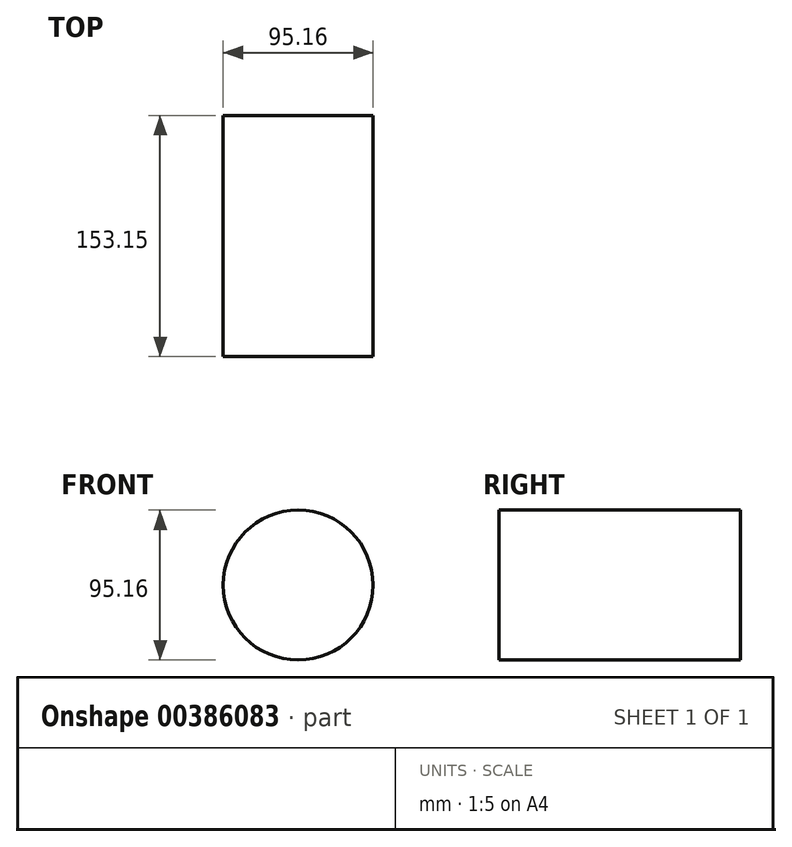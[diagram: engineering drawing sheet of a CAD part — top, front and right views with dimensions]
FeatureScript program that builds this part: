
annotation { "Feature Type Name" : "Feature", "Feature Type Description" : "" }
export const myFeature = defineFeature(function(context is Context, id is Id, definition is map)
    precondition{}
    {
        {
            var Q0;
            Q0=qCreatedBy(makeId("Top.planeOp"),FACE);
            var sketch = newSketch(context, id + "F0", { "sketchPlane" : qUnion([Q0])});
            skLineSegment(sketch, "E0", {"start": v(0, 0) * mm, "end": v(0, -50) * mm});
            skLineSegment(sketch, "E1", {"start": v(-50, 0) * mm, "end": v(0, 0) * mm});
            skSolve(sketch);
        }
        {
            var Q0;
            Q0=qCreatedBy(makeId("Right.planeOp"),FACE);
            var sketch = newSketch(context, id + "F1", { "sketchPlane" : qUnion([Q0])});
            skLineSegment(sketch, "E2.bottom", {"start": v(0, 50) * mm, "end": v(-25, 50) * mm});
            skLineSegment(sketch, "E2.top", {"start": v(0, 0) * mm, "end": v(-25, 0) * mm});
            skLineSegment(sketch, "E2.left", {"start": v(0, 50) * mm, "end": v(0, 0) * mm});
            skLineSegment(sketch, "E2.right", {"start": v(-25, 50) * mm, "end": v(-25, 0) * mm});
            skLineSegment(sketch, "E3.bottom", {"start": v(-23.1, -11.9) * mm, "end": v(23.1, -11.9) * mm});
            skLineSegment(sketch, "E3.top", {"start": v(-23.1, 11.9) * mm, "end": v(23.1, 11.9) * mm});
            skLineSegment(sketch, "E3.left", {"start": v(-23.1, -11.9) * mm, "end": v(-23.1, 11.9) * mm});
            skLineSegment(sketch, "E3.right", {"start": v(23.1, -11.9) * mm, "end": v(23.1, 11.9) * mm});
            skPoint(sketch, "E3.middle", {"position": v(0, 0) * mm});
            skCircle(sketch, "E4", {"center": v(0, 0) * mm, "radius": 25.98 * mm});
            skSolve(sketch);
        }
        {
            var Q0;
            {var subQ0=sQuery(id+"F1.wireOp",EDGE,"E4");var subQ1=sQuery(id+"F1.wireOp",EDGE,"E2.left");var subQ2=makeQuery(id+"F1.imprint","INTERSECT",VERTEX,{"derivedFrom":[subQ1,subQ0]});Q0=makeQuery(id+"F1.imprint","IMPRINT",FACE,{"disambiguationData":[TD([[makeQuery(id+"F1.imprint","IMPRINT",EDGE,{"disambiguationData":[TD([[subQ2,-1.0]])],"derivedFrom":subQ1}),1.0]])]});}
            var Q1;
            Q1=sQuery(id+"F1.wireOp",EDGE,"E3.top");
            revolve(context, id + "F2", {"entities" : qUnion([Q0]), "axis" : qUnion([Q1]), "revolveType" : RevolveType.FULL});
        }
        {
            var Q0;
            Q0=sQuery(id+"F0.wireOp",EDGE,"E0");
            extrude(context, id + "F3", {"bodyType" : ToolBodyType.SURFACE, "surfaceEntities" : qUnion([Q0]), "endBound" : BoundingType.SYMMETRIC, "depth" : 22 * mm});
        }
        {
            var Q0;
            Q0=qCreatedBy(makeId("Front.planeOp"),FACE);
            var sketch = newSketch(context, id + "F4", { "sketchPlane" : qUnion([Q0])});
            skCircle(sketch, "E5", {"center": v(0, 0) * mm, "radius": 47.58 * mm});
            skPoint(sketch, "E5.first.point", {"position": v(-23.16, -41.56) * mm});
            skPoint(sketch, "E5.second.point", {"position": v(46.66, 9.32) * mm});
            skPoint(sketch, "E5.third.point", {"position": v(-21, 42.7) * mm});
            skSolve(sketch);
        }
        {
            var Q0;
            Q0 = qSketchRegion(id + "F4", true);
            extrude(context, id + "F5", {"entities" : qUnion([Q0]), "operationType" : NewBodyOperationType.ADD, "endBound" : BoundingType.THROUGH_ALL, "oppositeDirection" : true, "depth" : 17.9 * mm});
        }
    });
